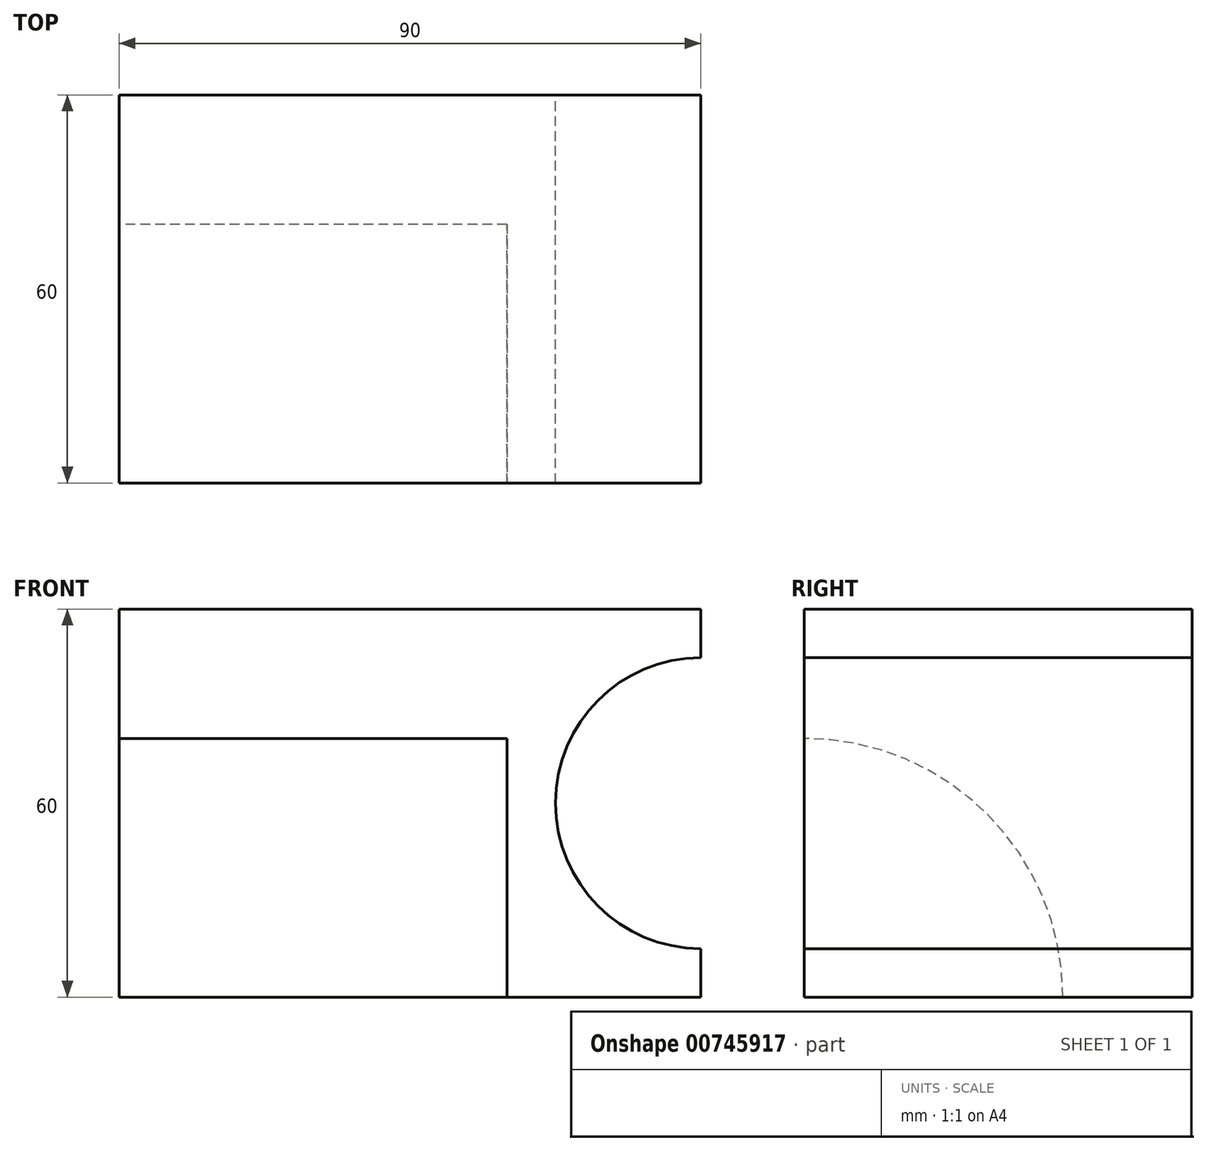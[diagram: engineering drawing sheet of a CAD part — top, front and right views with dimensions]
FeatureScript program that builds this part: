
annotation { "Feature Type Name" : "Feature", "Feature Type Description" : "" }
export const myFeature = defineFeature(function(context is Context, id is Id, definition is map)
    precondition{}
    {
        {
            var Q0;
            Q0=qCreatedBy(makeId("Front.planeOp"),FACE);
            var sketch = newSketch(context, id + "F0", { "sketchPlane" : qUnion([Q0])});
            skLineSegment(sketch, "E0", {"start": v(0, 0) * mm, "end": v(0, 60) * mm});
            skLineSegment(sketch, "E1", {"start": v(0, 60) * mm, "end": v(30, 60) * mm});
            skLineSegment(sketch, "E2", {"start": v(30, 60) * mm, "end": v(30, 0) * mm});
            skLineSegment(sketch, "E3", {"start": v(30, 0) * mm, "end": v(0, 0) * mm});
            skArc(sketch, "E4", {"start": v(30, 52.5) * mm, "mid": v(7.5, 30) * mm, "end": v(30, 7.5) * mm});
            skSolve(sketch);
        }
        {
            var Q0;
            Q0=makeQuery(id+"F0.imprint","IMPRINT",FACE,{"disambiguationData":[TD([[makeQuery(id+"F0.imprint","IMPRINT",EDGE,{"derivedFrom":sQuery(id+"F0.wireOp",EDGE,"E0")}),-1.0]])]});
            extrude(context, id + "F1", {"entities" : qUnion([Q0]), "depth" : 60 * mm, "offsetDistance" : 25 * mm});
        }
        {
            var Q0;
            Q0=makeQuery(id+"F1.opExtrude","CAP_FACE",FACE,{"disambiguationData":[OSD([sQuery(id+"F0.wireOp",EDGE,"E0"),sQuery(id+"F0.wireOp",EDGE,"E1"),sQuery(id+"F0.wireOp",EDGE,"E2"),sQuery(id+"F0.wireOp",EDGE,"E3"),sQuery(id+"F0.wireOp",EDGE,"E4")])],"isStart":false});
            var sketch = newSketch(context, id + "F2", { "sketchPlane" : qUnion([Q0])});
            skLineSegment(sketch, "E5", {"start": v(0, 60) * mm, "end": v(-60, 60) * mm});
            skLineSegment(sketch, "E6", {"start": v(-60, 60) * mm, "end": v(-60, 0) * mm});
            skLineSegment(sketch, "E7", {"start": v(-60, 0) * mm, "end": v(0, 0) * mm});
            skSolve(sketch);
        }
        {
            var Q0;
            Q0=makeQuery(id+"F2.imprint","IMPRINT",FACE,{"disambiguationData":[TD([[makeQuery(id+"F2.imprint","IMPRINT",EDGE,{"derivedFrom":sQuery(id+"F2.wireOp",EDGE,"E5")}),1.0]])]});
            extrude(context, id + "F3", {"entities" : qUnion([Q0]), "operationType" : NewBodyOperationType.ADD, "oppositeDirection" : true, "depth" : 60 * mm, "offsetDistance" : 25 * mm});
        }
        {
            var Q0;
            Q0=makeQuery(id+"F3.opExtrude","SWEPT_FACE",FACE,{"disambiguationData":[OSD([sQuery(id+"F2.wireOp",EDGE,"E6")])]});
            var sketch = newSketch(context, id + "F4", { "sketchPlane" : qUnion([Q0])});
            skArc(sketch, "E8", {"start": v(60, 40) * mm, "mid": v(31.72, 28.28) * mm, "end": v(20, 0) * mm});
            skSolve(sketch);
        }
        {
            var Q0;
            {var subQ0=sQuery(id+"F4.wireOp",EDGE,"E8");Q0=makeQuery(id+"F4.imprint","IMPRINT",FACE,{"disambiguationData":[TD([[makeQuery(id+"F4.imprint","IMPRINT",EDGE,{"derivedFrom":subQ0}),1.0]])]});}
            extrude(context, id + "F5", {"entities" : qUnion([Q0]), "operationType" : NewBodyOperationType.REMOVE, "oppositeDirection" : true, "depth" : 60 * mm, "offsetDistance" : 25 * mm});
        }
    });
